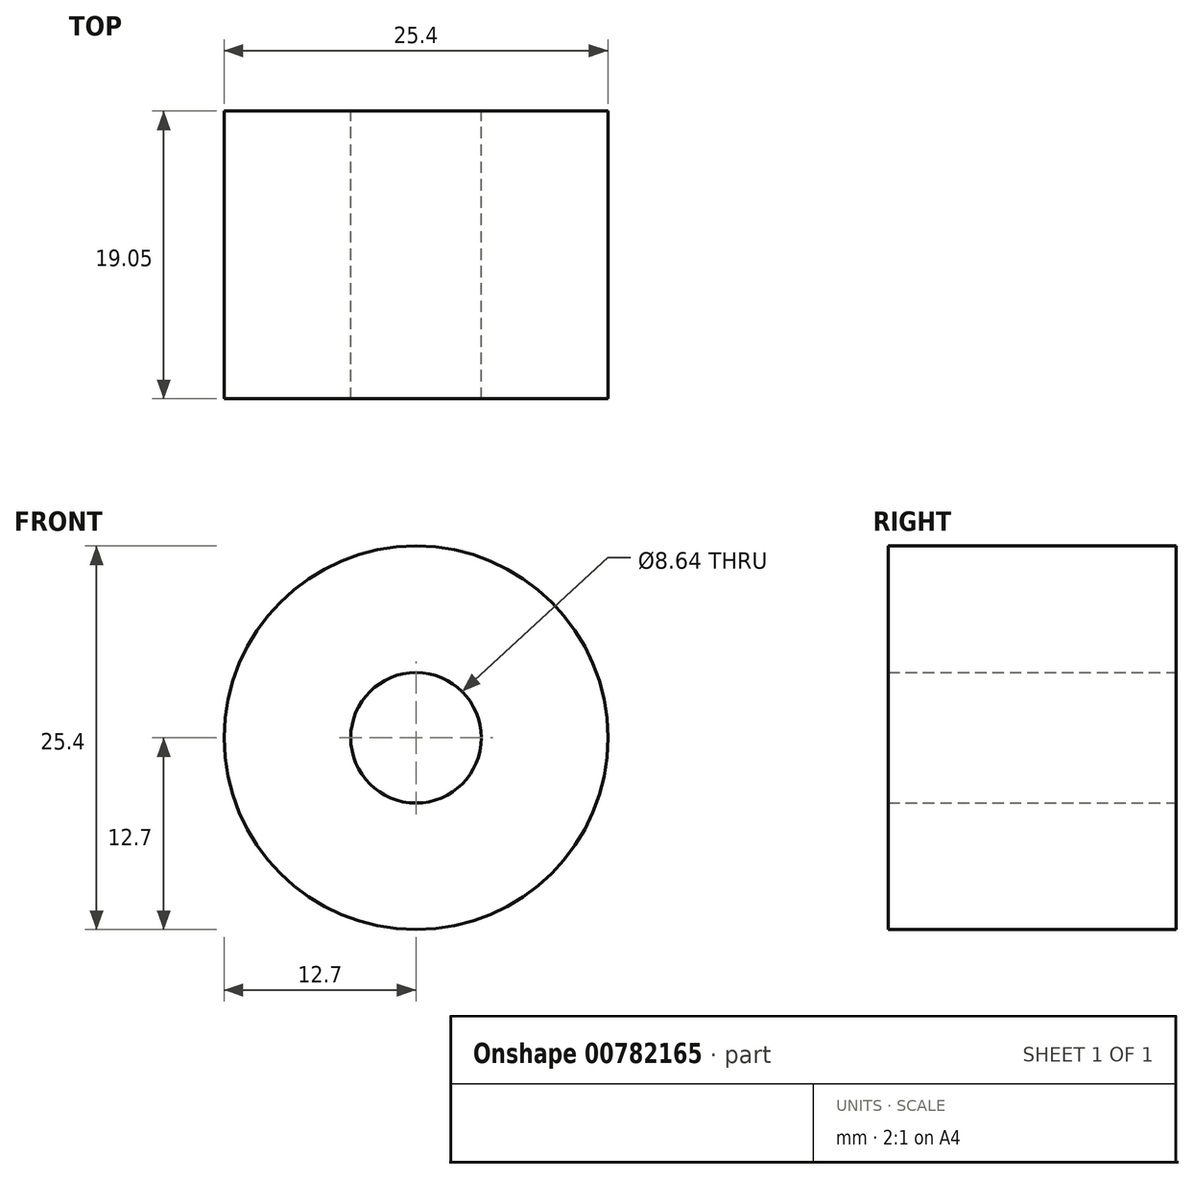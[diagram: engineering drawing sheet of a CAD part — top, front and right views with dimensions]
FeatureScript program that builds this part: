
annotation { "Feature Type Name" : "Feature", "Feature Type Description" : "" }
export const myFeature = defineFeature(function(context is Context, id is Id, definition is map)
    precondition{}
    {
        {
            var Q0;
            Q0=qCreatedBy(makeId("Front.planeOp"),FACE);
            var sketch = newSketch(context, id + "F0", { "sketchPlane" : qUnion([Q0])});
            skCircle(sketch, "E0", {"center": v(0, 0) * mm, "radius": 4.32 * mm});
            skCircle(sketch, "E1", {"center": v(0, 0) * mm, "radius": 12.7 * mm});
            skSolve(sketch);
        }
        {
            var Q0;
            Q0=qSketchRegion(id+"F0",true);
            extrude(context, id + "F1", {"entities" : qUnion([Q0]), "depth" : 19.05 * mm, "offsetDistance" : 25.4 * mm});
        }
    });
